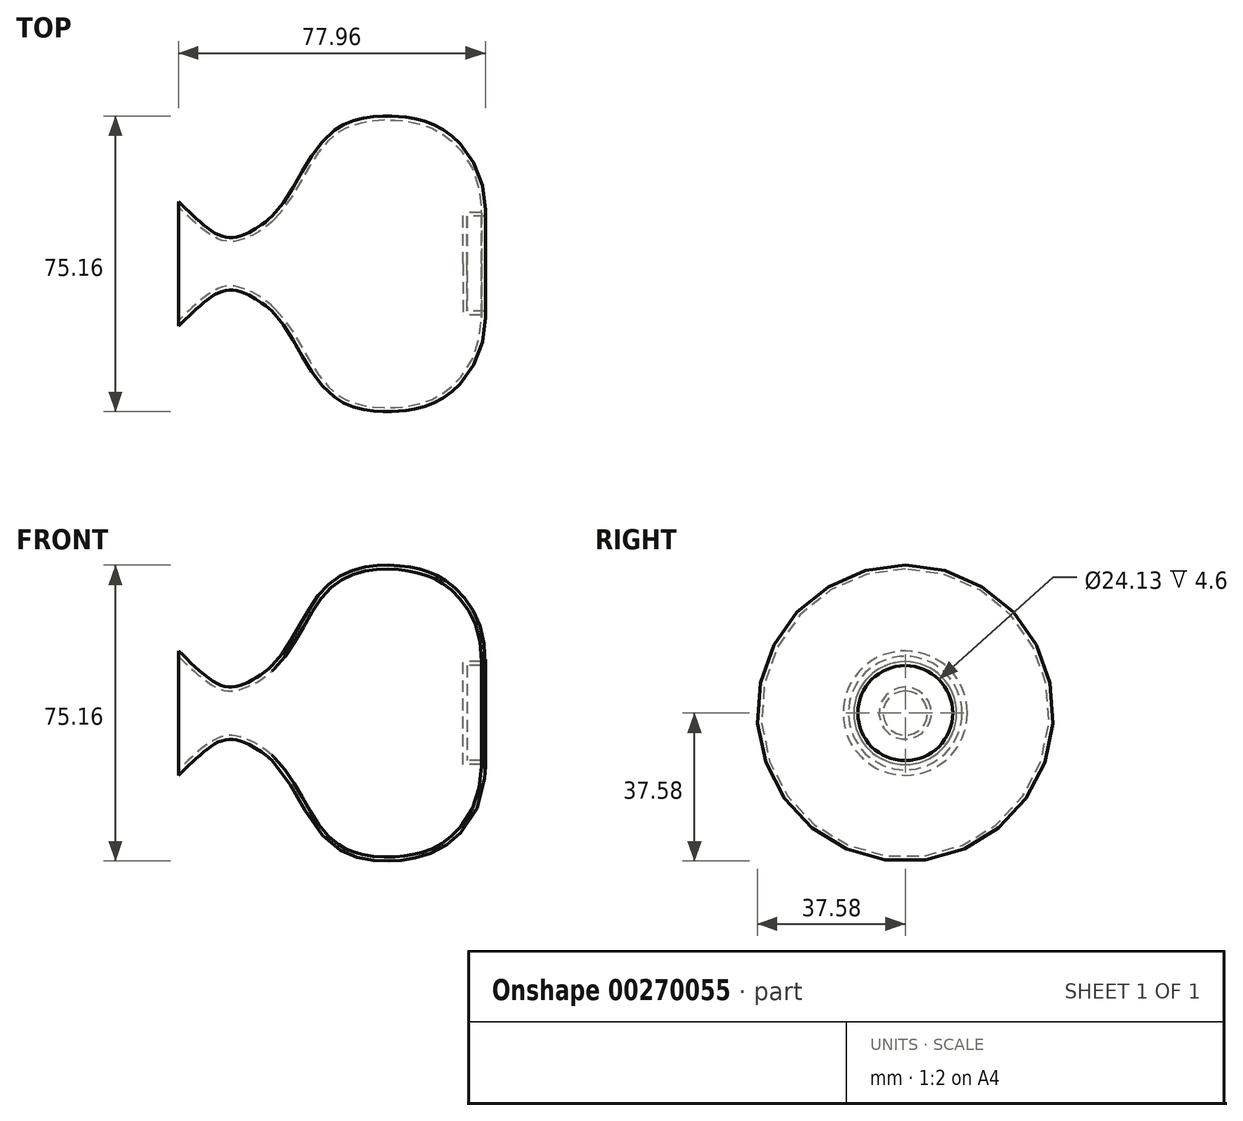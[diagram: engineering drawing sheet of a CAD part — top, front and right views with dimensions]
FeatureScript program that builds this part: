
annotation { "Feature Type Name" : "Feature", "Feature Type Description" : "" }
export const myFeature = defineFeature(function(context is Context, id is Id, definition is map)
    precondition{}
    {
        {
            var Q0;
            Q0=qCreatedBy(makeId("Top.planeOp"),FACE);
            var sketch = newSketch(context, id + "F0", { "sketchPlane" : qUnion([Q0])});
            skLineSegment(sketch, "E0", {"start": v(-35.37, 0) * mm, "end": v(-35.37, 15.8) * mm});
            skFitSpline(sketch, "E1", {"points": [v(-11.6, 12.07) * mm, v(2.24, 32.2) * mm, v(16.07, 37.55) * mm, v(25.78, 36.58) * mm, v(33.53, 32.95) * mm, v(42.55, 12.07) * mm], "startDerivative": vector(62.37, 59.81) * mm, "endDerivative": vector(-6.58, -135.5) * mm});
            skLineSegment(sketch, "E2", {"start": v(-35.37, 0) * mm, "end": v(37.95, 0) * mm});
            skFitSpline(sketch, "E3", {"points": [v(-35.37, 15.8) * mm, v(-25.49, 7.5) * mm, v(-19.44, 7.14) * mm, v(-11.6, 12.07) * mm], "startDerivative": vector(22.3, -20.79) * mm, "endDerivative": vector(20.33, 19.73) * mm});
            skPoint(sketch, "E4.start.orphan", {"position": v(50.94, 0) * mm});
            skLineSegment(sketch, "E5", {"start": v(42.55, 12.07) * mm, "end": v(37.95, 12.07) * mm});
            skLineSegment(sketch, "E6", {"start": v(37.95, 12.07) * mm, "end": v(37.95, 0) * mm});
            skSolve(sketch);
        }
        {
            var Q0;
            Q0=makeQuery(id+"F0.imprint","IMPRINT",FACE,{"disambiguationData":[TD([[makeQuery(id+"F0.imprint","IMPRINT",EDGE,{"derivedFrom":sQuery(id+"F0.wireOp",EDGE,"E0")}),-1.0]])]});
            var Q1;
            Q1=sQuery(id+"F0.wireOp",EDGE,"E2");
            revolve(context, id + "F1", {"entities" : qUnion([Q0]), "axis" : qUnion([Q1]), "revolveType" : RevolveType.FULL});
        }
        {
            var Q0;
            Q0=makeQuery(id+"F1.opRevolve","SWEPT_FACE",FACE,{"disambiguationData":[OSD([sQuery(id+"F0.wireOp",EDGE,"E0")])]});
            shell(context, id + "F2", {"entities" : qUnion([Q0]), "thickness" : 1 * mm});
        }
    });
